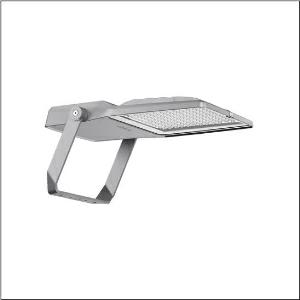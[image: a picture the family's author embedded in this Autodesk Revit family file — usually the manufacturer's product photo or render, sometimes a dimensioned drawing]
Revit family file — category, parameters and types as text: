
# Revit family: floodlight_fl_21_iq_midi___rs12_5xa7781e4b1a_82bf
name_source: partatom
category: Lighting Fixtures
units: mm (PartAtom-declared; Revit-internal decimal feet)

## family parameters
Cut with Voids When Loaded = No
Host = Face
Light Source = No
Part Type = Normal
Room Calculation Point = No
Round Connector Dimension = Use Diameter
Shared = No

## types (1)
- --- (1 x LED, 27880 lm, 208.1 W, 4000K)
    Apparent Load = 208 VA
    CIE Flux Codes = 79 92 99 100 100
    Color Rendering = 70
    Color Temperature = 4000K
    Default Elevation = 1800 mm
    Description = Floodlight FL 21 iQ midi, floodlight, primary light control with lens, of PMMA, primary optical cover: protective disc, of toughened safety glass, transparent, light distribution: RS12, light emission: direct distribution, installation type: surface-mounted, LED, High Power LED, rated luminous flux: 27.880lm, luminous efficacy: 134lm/W, light colour: 740, colour temperature: 4000K, control gear: ECG iQ, control: optimised constant luminous flux control (CLO 2.0), Desk-Remote (wireless, voltage-free reading and setting of iQ features in the workshop via application-optimized NFC function/RFID function), Light-Fading, Smart-Wire, Night-Set, Lumen-Switch, Temp-Guard, Auto-Match, with terminal, 6-pole, mains connection: 220..240V, AC, 50/60Hz, start of lifetime: 208W, end of service life: 227W, reduction: 90W, luminaire housing, of diecast aluminium, powder-coated, Siteco® metallic grey (DB 702S), corrosivity category C5 mid according to DIN EN ISO 12944, sealing non-destructively replaceable, mounting bracket, of steel, galvanised, powder-coated, Siteco® metallic grey (DB 702S), protection rating (complete): IP66, insulation class (complete): insulation class II (safety insulation), certification: CE, protection symbol: D, impact resistance: IK08, permissible operating ambient temperature: -40..+40°C, permissible operating ambient temperature for outdoor applications: -40..+50°C, standard: DIN EN 12944, LABS conformity tested according to VDMA 24364:2018-05, packaging unit: 1 piece

Light Distribution: RS12
    Height = 76 mm
    Lamp = 1 x LED
    Lamp Light Flux = 27880 lm
    Lamp Power = 208.1 W
    Lamp count = 1
    Length = 657 mm
    Luminous efficacy = 134 lm/W
    Manufacturer = Siteco
    ModVariant = No
    Model = 5XA7781E4B1A
    Number of Poles = 1
    OnlyDefault = Yes
    Power Factor = 1
    Product Name = Floodlight FL 21 iQ midi | RS12
    Product group = floodlight | pylon annexe
    ProductGroupID = 6200
    Protection Class = Protection class II
    Protection Degree = IP 66
    RLX_Detail_Level = 1
    RLX_Emergency_Light_Flux = 0 lm
    RLX_Emergency_Type = 0
    RLX_Emergency_Type_DB = No
    RlxData = <blob elided: 141361 chars, md5=ccbce5fe>
    Socket = socket
    Standby Power = 0 W
    System Light Flux = 27880 lm
    System Power = 208 W
    Type Comments = factory setting: luminous flux: 100 % | dim-lin: 254 | 710 mA
    Type Image = l_1006876.jpg
    URL = http://relux.com
    VarID = @adj_056179
    Voltage = 0 V
    Weight = 0.00 kg
    Width = 442 mm

## geometry (parser evidence)
native form markers: Blend x4, Sweep x13
no freeform markers — native parametric forms only
